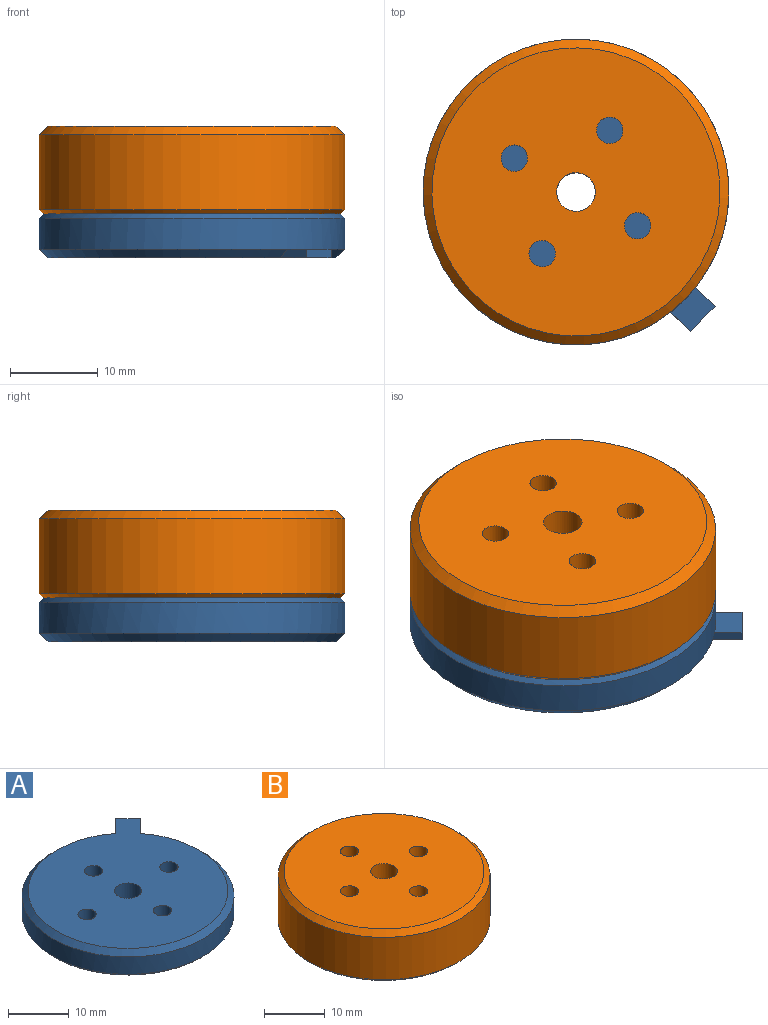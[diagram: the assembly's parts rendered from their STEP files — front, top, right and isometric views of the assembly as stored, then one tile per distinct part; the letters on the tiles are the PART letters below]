
ASSEMBLY  parts=2 mates=1
PART A: 14 faces, bbox 34.8x34.8x5 mm
  f0: cone r=16.4mm half-angle=45deg, axis (0,0,-1), area 144.5mm2, adj f6,f7,f10,f12
  f1: cylinder r=2.2mm len=5mm, axis (0,0,-1), area 69.1mm2, adj f7,f8
  f2: cylinder r=1.5mm len=5mm, axis (0,0,-1), area 47.1mm2, adj f7,f8
  f3: cylinder r=1.5mm len=5mm, axis (0,0,-1), area 47.1mm2, adj f7,f8
  f4: cylinder r=1.5mm len=5mm, axis (0,0,-1), area 47.1mm2, adj f7,f8
  f5: cylinder r=1.5mm len=5mm, axis (0,0,-1), area 47.1mm2, adj f7,f8
  f6: cylinder r=17.4mm len=34.8mm, axis (0,0,-1), area 382.6mm2, adj f0,f9,f13
  f7: plane 32.8x32.8mm, normal (0,0,1), area 817.6mm2, adj f0,f1,f2,f3,f4,f5,f10,f11
  f8: plane 33.8x33.8mm, normal (0,0,-1), area 853.8mm2, adj f1,f2,f3,f4,f5,f9
  f9: cone r=17.4mm half-angle=45deg, axis (0,0,1), area 76.2mm2, adj f6,f8
  f10: plane 2.92x2.92mm, normal (0.71,-0.71,0), area 3.6mm2, adj f0,f7,f11,f13
  f11: plane 2.83x2.83mm, normal (0.71,0.71,0), area 4mm2, adj f7,f10,f12,f13
  f12: plane 2.92x2.92mm, normal (-0.71,0.71,0), area 3.6mm2, adj f0,f7,f11,f13
  f13: plane 5.03x5.03mm, normal (0,0,-1), area 12.2mm2, adj f6,f10,f11,f12
PART B: 10 faces, bbox 34.8x34.8x10 mm
  f0: cylinder r=2.2mm len=10mm, axis (0,0,-1), area 138.2mm2, adj f6,f7
  f1: cylinder r=1.5mm len=10mm, axis (0,0,-1), area 94.2mm2, adj f6,f7
  f2: cylinder r=1.5mm len=10mm, axis (0,0,-1), area 94.2mm2, adj f6,f7
  f3: cylinder r=1.5mm len=10mm, axis (0,0,-1), area 94.2mm2, adj f6,f7
  f4: cylinder r=1.5mm len=10mm, axis (0,0,-1), area 94.2mm2, adj f6,f7
  f5: cylinder r=17.4mm len=34.8mm, axis (0,0,-1), area 929.3mm2, adj f8,f9
  f6: plane 32.8x32.8mm, normal (0,0,1), area 801.5mm2, adj f0,f1,f2,f3,f4,f8
  f7: plane 33.8x33.8mm, normal (0,0,-1), area 853.8mm2, adj f0,f1,f2,f3,f4,f9
  f8: cone r=16.4mm half-angle=45deg, axis (0,0,-1), area 150.2mm2, adj f5,f6
  f9: cone r=17.4mm half-angle=45deg, axis (0,0,1), area 76.2mm2, adj f5,f7
PLACE A rot(axis=(1,0,0),180deg) t=(-3.14,-2.53,-2.3)mm fixed
PLACE B rot(axis=(0,0,1),61.2deg) t=(-3.14,-2.53,-2.3)mm
MATE revolute A.f0 <-> B.f0  axis (0,0,1) through (-3.14,-2.53,-2.3)mm
